# Revit family: CombinationUnit_Recessed_ASIJDMacDonald_HandDryer_PaperDispenser_WasteBin_26L
name_source: partatom
category: Specialty Equipment
revit_build: Autodesk Revit 2016 (Build: 20190508_0715(x64)
units: mm (PartAtom-declared; Revit-internal decimal feet)

## family parameters
Always vertical = Yes
Cut with Voids When Loaded = Yes
OmniClass Number = 23.40.20.21.17
OmniClass Title = Paper Towel Dispensers, Disposal Units
Part Type = Normal
Room Calculation Point = No
Round Connector Dimension = Use Diameter
Shared = No
Work Plane-Based = No

## types (3) — shared parameters
Manufacturer = ASI JD MacDonald
Manufacturer_Overall Depth = 191 mm
Manufacturer_Overall Height = 1407 mm
Manufacturer_Overall Width = 391 mm
Manufacturer_URL__Product Specific = https://jdmacdonald.com.au
ModifiedIssue_ANZRS = 20190912 $
URL = www.asijdmacdonald.com.au
Voltage = 240 V
zero-valued in all types: Cost

## per-type parameters (varying)
| type | Body Material | Description | Manufacturer_Spec Code | Model | Type Comments |
| Stainless Steel (10-64672-2) | z_ASI JD MacDonald_Stainless Steel | Turbo 3 In 1 Paper Towel Dispenser, High-Speed Hand Dryer & Waste Bin – Simplicity Collection (10-64672-2) | 10-64672-2 | 10-64672-2 | Combination Unit - Recessed - Hand Dryer & Paper Dispenser & Waste Bin - 26L - Satin Stainless Steel |
| Piatto Black (10-64672-2-41) | z_ASI JD MacDonald_Piatto Black | Turbo 3 In 1 Paper Towel Dispenser, High-Speed Hand Dryer & Waste Bin – Completely Recessed, Matte Black Phenolic Door, Piatto™ Collection (10-64672-2-41) | 10-64672-2-41 | 10-64672-2-41 | Combination Unit - Recessed - Hand Dryer & Paper Dispenser & Waste Bin - 26L - Matte Black
Combination Unit - Recessed - Hand Dryer & Paper Dispenser & Waste Bin - 26L - Matte Black
Combination Unit - Recessed - Hand Dryer & Paper Dispenser & Waste Bin - 26L - Matte Black
Combination Unit - Recessed - Hand Dryer & Paper Dispenser & Waste Bin - 26L - Matte Black |
| Piatto White (10-64672-2-00) | z_ASI JD MacDonald_Piatto White | Turbo 3 In 1 Paper Towel Dispenser, High-Speed Hand Dryer & Waste Bin – Completely Recessed, White Phenolic Door, Piatto™ Collection (10-64672-2-00) | 10-64672-2-00 | 10-64672-2-00 | Combination Unit - Recessed - Hand Dryer & Paper Dispenser & Waste Bin - 26L - White |

## geometry (parser evidence)
native form markers: Sweep x3
no freeform markers — native parametric forms only
